# Revit family: xFaucet-Soap_Dispenser-Sloan-ESD-601
name_source: partatom
category: Plumbing Fixtures
revit_build: Autodesk Revit 2014 (Build: 20130308_1515(x64)
units: mm (PartAtom-declared; Revit-internal decimal feet)

## types (1)
- ESD-601
    ADA Compliant = Yes
    Assembly Code = D2010
    CW Connection = Yes
    CWFU = 1.5
    CalGreen Compliant = Yes
    Code Number = 3346090
    Cold Water Connection Diameter = 3/8"
    Default Elevation = 0"
    Description = Faucet and Soap Dispenser Combination
    Faucet Type = Faucet-Battery-Sloan-Optima_Plus-EBF-615-4 : EBF-615-4
    Flow Rate = 0.5 gpm (1.9 Lpm)
    HW Connection = Yes
    HWFU = 1.5
    Hot Water Connection Diameter = 0"
    IAPMO Compliance = cUPC
    Installation Type = Deck Mounted
    Manufacturer = SLOAN
    Material = Metal-Sloan-Chrome Plated
    Model = ESD-601
    Operation = Sensor Activated
    Price = Prices may vary. Please consult Manufacturer Representative for most up-to-date price list.
    Product Documentation Link = https://specifications.sloan.com
    Product Page URL = https://www.sloan.com
    Soap Dispenser Installation Width = 6"
    Soap Dispenser Offset = 1/2"
    Soap Dispenser Type = Soap_Dispenser-Sloan-ESD-600 : ESD-600
    URL = https://www.sloan.com
    Vent Connection = No
    Voltage = 120 V
    WFU = 0
    Warranty Information = 3 Year Limited Warranty
    Waste Connection = No

## geometry (parser evidence)
native form markers: Sweep x6
no freeform markers — native parametric forms only
